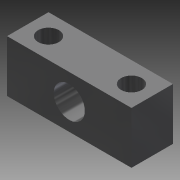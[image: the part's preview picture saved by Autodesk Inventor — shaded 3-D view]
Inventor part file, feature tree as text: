
AUTODESK INVENTOR PART (.ipt)
format: ipt  version: 2012 (Build 160160000, 160)  size: 93,184 bytes
history: native  units: in
note: dims shown in document units (in); Inventor stores cm internally (conversion verified against a paired STEP export)
features: extrude x2, sketch x2
ambient origin geometry x8: Origin, YZ Plane, XZ Plane, XY Plane, X Axis, Y Axis, Z Axis, Center Point
bodies: Solid1 (feature_tree)
feature tree (4):
  extrude  "Extrusion1"  Depth=1.5in
  extrude  "Extrusion2"  Depth=0.5in TaperAngle=0.0deg
  sketch  "Sketch1"  dims[d0=0.625in d1=1.5in]
  sketch  "Sketch2"  dims[d2=0.375in d3=0.5in d4=0.0in d5=0.3125in d6=0.25in d7=0.25in d8=0.25in d9=0.25in d10=0.5in d11=0.0in]
